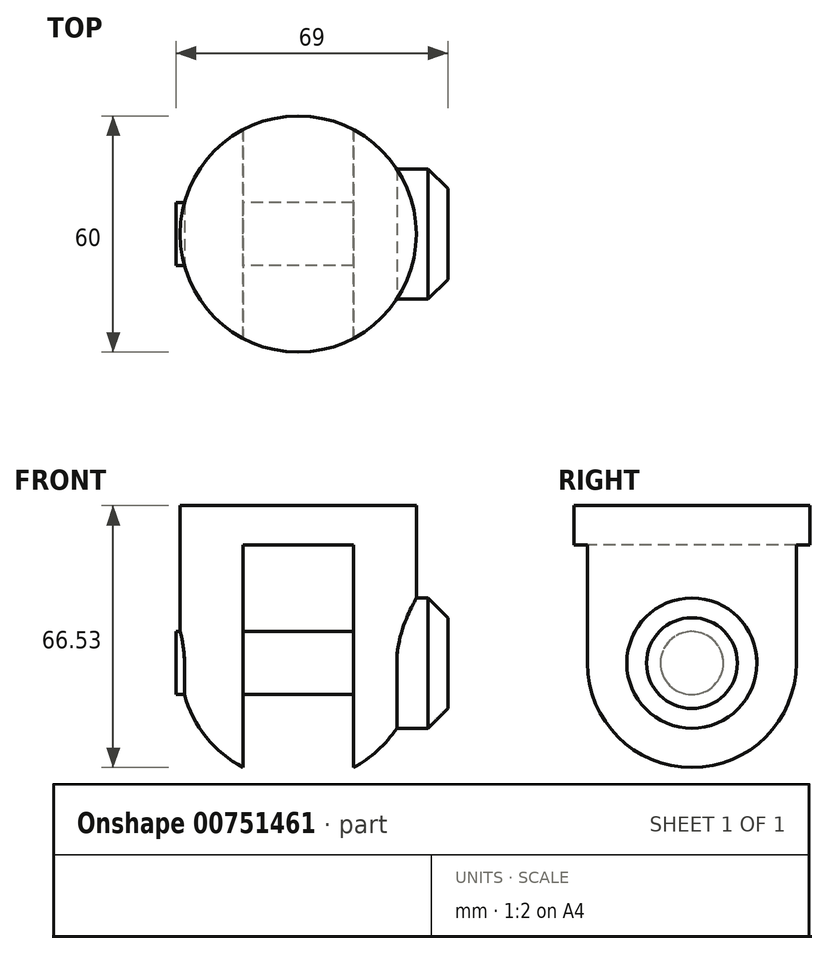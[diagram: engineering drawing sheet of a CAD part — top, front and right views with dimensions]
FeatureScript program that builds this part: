
annotation { "Feature Type Name" : "Feature", "Feature Type Description" : "" }
export const myFeature = defineFeature(function(context is Context, id is Id, definition is map)
    precondition{}
    {
        {
            var Q0;
            Q0=qCreatedBy(makeId("Front.planeOp"),FACE);
            var sketch = newSketch(context, id + "F0", { "sketchPlane" : qUnion([Q0])});
            skLineSegment(sketch, "E0", {"start": v(0, 0) * mm, "end": v(30, 0) * mm});
            skLineSegment(sketch, "E1", {"start": v(30, 0) * mm, "end": v(30, -40) * mm});
            skArc(sketch, "E2", {"start": v(0, -70) * mm, "mid": v(21.21, -61.21) * mm, "end": v(30, -40) * mm});
            skLineSegment(sketch, "E3", {"start": v(0, 0) * mm, "end": v(0, -70) * mm});
            skLineSegment(sketch, "E4", {"start": v(0, 0) * mm, "end": v(0, 8.72) * mm, "construction": true});
            skLineSegment(sketch, "E5", {"start": v(0, -40) * mm, "end": v(30, -40) * mm, "construction": true});
            skArc(sketch, "E6", {"start": v(30, -40) * mm, "mid": v(21.21, -18.79) * mm, "end": v(0, -10) * mm, "construction": true});
            skLineSegment(sketch, "E7", {"start": v(0, -10) * mm, "end": v(30, -10) * mm, "construction": true});
            skLineSegment(sketch, "E8", {"start": v(14, -10) * mm, "end": v(14, -70) * mm, "construction": true});
            skLineSegment(sketch, "E9", {"start": v(14, -70) * mm, "end": v(0, -70) * mm, "construction": true});
            skSolve(sketch);
        }
        {
            var Q0;
            Q0 = qSketchRegion(id + "F0", true);
            var Q1;
            Q1=sQuery(id+"F0.wireOp",EDGE,"E4");
            revolve(context, id + "F1", {"surfaceOperationType" : NewSurfaceOperationType.NEW, "entities" : qUnion([Q0]), "axis" : qUnion([Q1]), "revolveType" : RevolveType.FULL});
        }
        {
            var Q0;
            Q0=qCreatedBy(makeId("Front.planeOp"),FACE);
            var sketch = newSketch(context, id + "F2", { "sketchPlane" : qUnion([Q0])});
            skLineSegment(sketch, "E10", {"start": v(14, -70) * mm, "end": v(14, -10) * mm});
            skLineSegment(sketch, "E11", {"start": v(14, -10) * mm, "end": v(0, -10) * mm});
            skLineSegment(sketch, "E12", {"start": v(0, -10) * mm, "end": v(0, -70) * mm, "construction": true});
            skLineSegment(sketch, "E13", {"start": v(0, -70) * mm, "end": v(14, -70) * mm});
            skLineSegment(sketch, "E14.MirrorCS", {"start": v(0, -70) * mm, "end": v(-14, -70) * mm});
            skLineSegment(sketch, "E15.MirrorCS", {"start": v(-14, -70) * mm, "end": v(-14, -10) * mm});
            skLineSegment(sketch, "E16.MirrorCS", {"start": v(-14, -10) * mm, "end": v(0, -10) * mm});
            skSolve(sketch);
        }
        {
            var Q0;
            Q0 = qSketchRegion(id + "F2", true);
            extrude(context, id + "F3", {"entities" : qUnion([Q0]), "operationType" : NewBodyOperationType.REMOVE, "endBound" : BoundingType.THROUGH_ALL, "oppositeDirection" : true, "depth" : 25 * mm, "offsetDistance" : 25 * mm, "hasSecondDirection" : true, "secondDirectionBound" : SecondDirectionBoundingType.THROUGH_ALL, "secondDirectionOppositeDirection" : false, "secondDirectionDepth" : 25 * mm});
        }
        {
            var Q0;
            Q0=qCreatedBy(makeId("Right.planeOp"),FACE);
            var sketch = newSketch(context, id + "F4", { "sketchPlane" : qUnion([Q0])});
            skCircle(sketch, "E17", {"center": v(0, -40) * mm, "radius": 8 * mm});
            skSolve(sketch);
        }
        {
            var Q0;
            Q0 = qSketchRegion(id + "F4", true);
            var Q1;
            Q1=sQuery(id+"F0.wireOp",VERTEX,"E1.end");
            extrude(context, id + "F5", {"entities" : qUnion([Q0]), "operationType" : NewBodyOperationType.ADD, "endBound" : BoundingType.UP_TO_VERTEX, "depth" : 25 * mm, "endBoundEntityVertex" : qUnion([Q1]), "hasOffset" : true, "offsetDistance" : 1 * mm, "offsetOppositeDirection" : true});
        }
        {
            var Q0;
            Q0=makeQuery(id+"F1.opRevolve","SWEPT_BODY",BODY,{"disambiguationData":[OSD([sQuery(id+"F0.wireOp",EDGE,"E0"),sQuery(id+"F0.wireOp",EDGE,"E1"),sQuery(id+"F0.wireOp",EDGE,"E2"),sQuery(id+"F0.wireOp",EDGE,"E3")])]});
            var Q1;
            Q1=qCreatedBy(makeId("Right.planeOp"),FACE);
            mirror(context, id + "F6", {"operationType" : NewBodyOperationType.ADD, "entities" : qUnion([Q0]), "mirrorPlane" : qUnion([Q1])});
        }
        {
            var Q0;
            Q0=makeQuery(id+"F5.opExtrude","CAP_FACE",FACE,{"disambiguationData":[OSD([sQuery(id+"F4.wireOp",EDGE,"E17")])],"isStart":false});
            var sketch = newSketch(context, id + "F7", { "sketchPlane" : qUnion([Q0])});
            skCircle(sketch, "E18", {"center": v(0, -40) * mm, "radius": 16.53 * mm});
            skSolve(sketch);
        }
        {
            var Q0;
            Q0 = qSketchRegion(id + "F7", true);
            var Q1;
            Q1=makeQuery(id+"F3.boolean.opBoolean","COPY",FACE,{"derivedFrom":makeQuery(id+"F3.opExtrude","SWEPT_FACE",FACE,{"disambiguationData":[OSD([sQuery(id+"F2.wireOp",EDGE,"E10")])]})});
            var Q2;
            Q2=makeQuery(id+"F1.opRevolve","SWEPT_BODY",BODY,{"disambiguationData":[OSD([sQuery(id+"F0.wireOp",EDGE,"E0"),sQuery(id+"F0.wireOp",EDGE,"E1"),sQuery(id+"F0.wireOp",EDGE,"E2"),sQuery(id+"F0.wireOp",EDGE,"E3")])]});
            extrude(context, id + "F8", {"entities" : qUnion([Q0]), "operationType" : NewBodyOperationType.ADD, "depth" : 7 * mm, "offsetDistance" : 25 * mm, "hasSecondDirection" : true, "secondDirectionBound" : SecondDirectionBoundingType.UP_TO_SURFACE, "secondDirectionOppositeDirection" : true, "secondDirectionDepth" : 25 * mm, "secondDirectionBoundEntityFace" : qUnion([Q1]), "secondDirectionBoundEntityBody" : qUnion([Q2])});
        }
        {
            var Q0;
            Q0=makeQuery(id+"F8.opExtrude","CAP_EDGE",EDGE,{"disambiguationData":[OSD([sQuery(id+"F7.wireOp",EDGE,"E18")])],"isStart":false});
            chamfer(context, id + "F9", {"entities" : qUnion([Q0]), "width" : 5 * mm, "tangentPropagation" : true});
        }
    });
